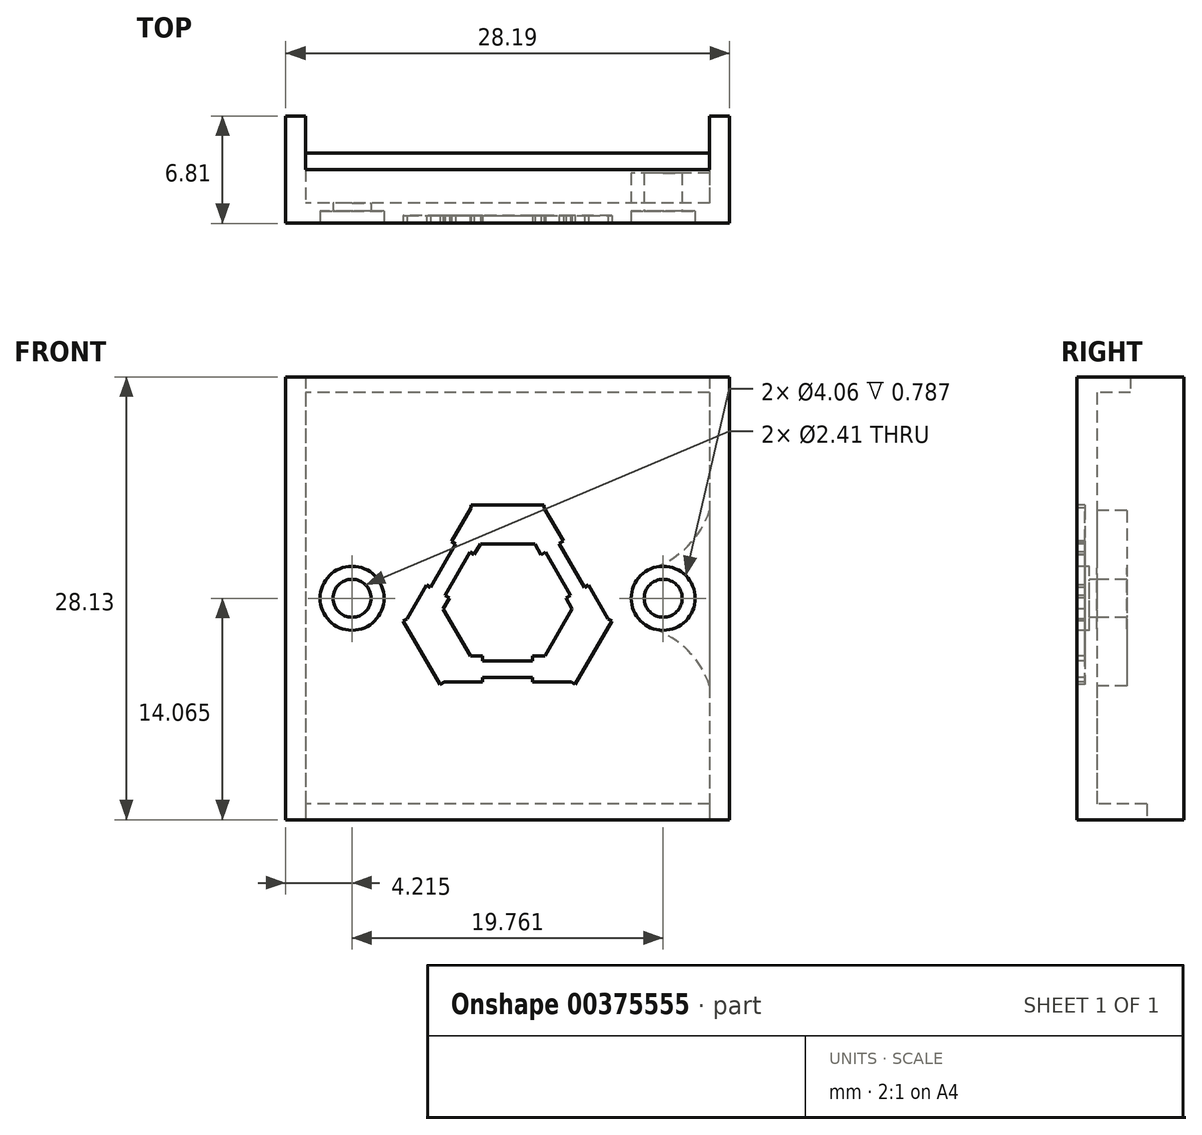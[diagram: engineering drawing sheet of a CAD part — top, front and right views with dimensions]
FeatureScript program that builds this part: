
annotation { "Feature Type Name" : "Feature", "Feature Type Description" : "" }
export const myFeature = defineFeature(function(context is Context, id is Id, definition is map)
    precondition{}
    {
        {
            var Q0;
            Q0=qCreatedBy(makeId("Top.planeOp"),FACE);
            var sketch = newSketch(context, id + "F0", { "sketchPlane" : qUnion([Q0])});
            skLineSegment(sketch, "E0", {"start": v(-22.88, 2.03) * mm, "end": v(-22.88, -1.6) * mm});
            skLineSegment(sketch, "E1", {"start": v(-22.88, -1.6) * mm, "end": v(2.77, -1.6) * mm});
            skLineSegment(sketch, "E2", {"start": v(2.77, -1.6) * mm, "end": v(2.77, 2.03) * mm});
            skLineSegment(sketch, "E3.0", {"start": v(4.04, -2.88) * mm, "end": v(4.04, 2.03) * mm});
            skLineSegment(sketch, "E3.1", {"start": v(-24.15, -2.88) * mm, "end": v(4.04, -2.88) * mm});
            skLineSegment(sketch, "E3.2", {"start": v(-24.15, 2.03) * mm, "end": v(-24.15, -2.88) * mm});
            skLineSegment(sketch, "E4", {"start": v(-24.15, 2.03) * mm, "end": v(-22.88, 2.03) * mm});
            skLineSegment(sketch, "E5", {"start": v(2.77, 2.03) * mm, "end": v(4.04, 2.03) * mm});
            skSolve(sketch);
        }
        {
            var Q0;
            Q0=makeQuery(id+"F0.imprint","IMPRINT",FACE,{"disambiguationData":[TD([[makeQuery(id+"F0.imprint","IMPRINT",EDGE,{"derivedFrom":sQuery(id+"F0.wireOp",EDGE,"E0")}),-1.0]])]});
            extrude(context, id + "F1", {"entities" : qUnion([Q0]), "depth" : 24.13 * mm});
        }
        {
            var Q0;
            Q0=makeQuery(id+"F1.opExtrude","SWEPT_FACE",FACE,{"disambiguationData":[OSD([sQuery(id+"F0.wireOp",EDGE,"E3.1")])]});
            var sketch = newSketch(context, id + "F2", { "sketchPlane" : qUnion([Q0])});
            skLineSegment(sketch, "E6", {"start": v(-10.05, 24.13) * mm, "end": v(-10.05, 0) * mm, "construction": true});
            skLineSegment(sketch, "E7", {"start": v(-19.94, 12.07) * mm, "end": v(-0.17, 12.07) * mm, "construction": true});
            skCircle(sketch, "E8", {"center": v(-19.94, 12.06) * mm, "radius": 2.03 * mm});
            skCircle(sketch, "E9", {"center": v(-0.17, 12.06) * mm, "radius": 2.03 * mm});
            skPoint(sketch, "E10.orphan", {"position": v(-24.15, 12.07) * mm});
            skPoint(sketch, "E11.orphan", {"position": v(4.04, 12.06) * mm});
            skPoint(sketch, "E12", {"position": v(-10.05, 12.06) * mm});
            skCircle(sketch, "E13", {"center": v(-19.94, 12.06) * mm, "radius": 1.2 * mm});
            skCircle(sketch, "E14", {"center": v(-0.17, 12.06) * mm, "radius": 1.2 * mm});
            skSolve(sketch);
        }
        {
            var Q0;
            Q0=makeQuery(id+"F2.imprint","IMPRINT",FACE,{"disambiguationData":[TD([[makeQuery(id+"F2.imprint","IMPRINT",EDGE,{"derivedFrom":sQuery(id+"F2.wireOp",EDGE,"E8")}),1.0]])]});
            var Q1;
            Q1=makeQuery(id+"F2.imprint","IMPRINT",FACE,{"disambiguationData":[TD([[makeQuery(id+"F2.imprint","IMPRINT",EDGE,{"derivedFrom":sQuery(id+"F2.wireOp",EDGE,"E9")}),1.0]])]});
            extrude(context, id + "F3", {"entities" : qUnion([Q0, Q1]), "operationType" : NewBodyOperationType.REMOVE, "oppositeDirection" : true, "depth" : 0.79 * mm});
        }
        {
            var Q0;
            Q0=makeQuery(id+"F3.boolean.opBoolean","SPLIT",FACE,{"disambiguationData":[TD([makeQuery(id+"F3.opExtrude","SWEPT_FACE",FACE,{"disambiguationData":[OSD([sQuery(id+"F2.wireOp",EDGE,"E13")])]})])],"derivedFrom":makeQuery(id+"F1.opExtrude","SWEPT_FACE",FACE,{"disambiguationData":[OSD([sQuery(id+"F0.wireOp",EDGE,"E3.1")])]})});
            var Q1;
            Q1=makeQuery(id+"F3.boolean.opBoolean","SPLIT",FACE,{"disambiguationData":[TD([makeQuery(id+"F3.opExtrude","SWEPT_FACE",FACE,{"disambiguationData":[OSD([sQuery(id+"F2.wireOp",EDGE,"E14")])]})])],"derivedFrom":makeQuery(id+"F1.opExtrude","SWEPT_FACE",FACE,{"disambiguationData":[OSD([sQuery(id+"F0.wireOp",EDGE,"E3.1")])]})});
            extrude(context, id + "F4", {"entities" : qUnion([Q0, Q1]), "operationType" : NewBodyOperationType.REMOVE, "oppositeDirection" : true, "depth" : 25.4 * mm});
        }
        {
            var Q0;
            {var subQ0=sQuery(id+"F0.wireOp",EDGE,"E3.0");var subQ4=sQuery(id+"F0.wireOp",EDGE,"E3.1");Q0=makeQuery(id+"F3.boolean.opBoolean","SPLIT",FACE,{"disambiguationData":[TD([makeQuery(id+"F1.opExtrude","SWEPT_FACE",FACE,{"disambiguationData":[OSD([subQ0])]})])],"derivedFrom":makeQuery(id+"F1.opExtrude","SWEPT_FACE",FACE,{"disambiguationData":[OSD([subQ4])]})});}
            var sketch = newSketch(context, id + "F5", { "sketchPlane" : qUnion([Q0])});
            skLineSegment(sketch, "E15", {"start": v(-10.05, 24.13) * mm, "end": v(-10.05, 0) * mm, "construction": true});
            skPoint(sketch, "E16", {"position": v(-10.05, 6.37) * mm});
            skLineSegment(sketch, "E17", {"start": v(-13.6, 15.68) * mm, "end": v(-12.4, 17.81) * mm});
            skLineSegment(sketch, "E18", {"start": v(-12.4, 17.81) * mm, "end": v(-12.4, 17.97) * mm});
            skLineSegment(sketch, "E19", {"start": v(-12.4, 17.97) * mm, "end": v(-7.74, 17.97) * mm});
            skLineSegment(sketch, "E20", {"start": v(-7.74, 17.97) * mm, "end": v(-7.74, 17.81) * mm});
            skLineSegment(sketch, "E21", {"start": v(-7.74, 17.81) * mm, "end": v(-6.51, 15.7) * mm});
            skLineSegment(sketch, "E22", {"start": v(-6.51, 15.7) * mm, "end": v(-6.78, 15.53) * mm});
            skLineSegment(sketch, "E23", {"start": v(-6.78, 15.53) * mm, "end": v(-5.18, 12.76) * mm});
            skLineSegment(sketch, "E24", {"start": v(-5.18, 12.76) * mm, "end": v(-4.92, 12.91) * mm});
            skLineSegment(sketch, "E25", {"start": v(-4.92, 12.91) * mm, "end": v(-3.68, 10.76) * mm});
            skLineSegment(sketch, "E26", {"start": v(-3.68, 10.76) * mm, "end": v(-3.44, 10.64) * mm});
            skLineSegment(sketch, "E27", {"start": v(-3.44, 10.64) * mm, "end": v(-5.76, 6.6) * mm});
            skLineSegment(sketch, "E28", {"start": v(-5.76, 6.6) * mm, "end": v(-6, 6.74) * mm});
            skLineSegment(sketch, "E29", {"start": v(-6, 6.74) * mm, "end": v(-8.47, 6.74) * mm});
            skLineSegment(sketch, "E30", {"start": v(-8.47, 6.74) * mm, "end": v(-8.47, 7.04) * mm});
            skLineSegment(sketch, "E31", {"start": v(-8.47, 7.04) * mm, "end": v(-11.65, 7.04) * mm});
            skLineSegment(sketch, "E32", {"start": v(-11.65, 7.04) * mm, "end": v(-11.65, 6.74) * mm});
            skLineSegment(sketch, "E33", {"start": v(-11.65, 6.74) * mm, "end": v(-14.07, 6.74) * mm});
            skLineSegment(sketch, "E34", {"start": v(-14.07, 6.74) * mm, "end": v(-14.35, 6.58) * mm});
            skLineSegment(sketch, "E35", {"start": v(-14.35, 6.58) * mm, "end": v(-16.68, 10.62) * mm});
            skLineSegment(sketch, "E36", {"start": v(-16.68, 10.62) * mm, "end": v(-16.45, 10.76) * mm});
            skLineSegment(sketch, "E37", {"start": v(-16.45, 10.76) * mm, "end": v(-15.22, 12.91) * mm});
            skLineSegment(sketch, "E38", {"start": v(-15.22, 12.91) * mm, "end": v(-14.94, 12.76) * mm});
            skLineSegment(sketch, "E39", {"start": v(-14.94, 12.76) * mm, "end": v(-13.35, 15.53) * mm});
            skLineSegment(sketch, "E40", {"start": v(-13.35, 15.53) * mm, "end": v(-13.6, 15.68) * mm});
            skLineSegment(sketch, "E41", {"start": v(-11.79, 15.5) * mm, "end": v(-8.33, 15.5) * mm});
            skLineSegment(sketch, "E42", {"start": v(-8.33, 15.5) * mm, "end": v(-7.94, 14.83) * mm});
            skLineSegment(sketch, "E43", {"start": v(-7.94, 14.83) * mm, "end": v(-7.65, 15) * mm});
            skLineSegment(sketch, "E44", {"start": v(-7.65, 15) * mm, "end": v(-6.06, 12.25) * mm});
            skLineSegment(sketch, "E45", {"start": v(-6.06, 12.25) * mm, "end": v(-6.36, 12.07) * mm});
            skLineSegment(sketch, "E46", {"start": v(-6.36, 12.07) * mm, "end": v(-5.97, 11.4) * mm});
            skLineSegment(sketch, "E47", {"start": v(-5.97, 11.4) * mm, "end": v(-7.69, 8.4) * mm});
            skLineSegment(sketch, "E48", {"start": v(-7.69, 8.4) * mm, "end": v(-8.47, 8.4) * mm});
            skLineSegment(sketch, "E49", {"start": v(-8.47, 8.4) * mm, "end": v(-8.47, 8.08) * mm});
            skLineSegment(sketch, "E50", {"start": v(-8.47, 8.08) * mm, "end": v(-11.64, 8.08) * mm});
            skLineSegment(sketch, "E51", {"start": v(-11.64, 8.08) * mm, "end": v(-11.64, 8.39) * mm});
            skLineSegment(sketch, "E52", {"start": v(-11.64, 8.39) * mm, "end": v(-12.41, 8.39) * mm});
            skLineSegment(sketch, "E53", {"start": v(-12.41, 8.39) * mm, "end": v(-14.15, 11.39) * mm});
            skLineSegment(sketch, "E54", {"start": v(-14.15, 11.39) * mm, "end": v(-13.76, 12.07) * mm});
            skLineSegment(sketch, "E55", {"start": v(-13.76, 12.07) * mm, "end": v(-14.04, 12.23) * mm});
            skLineSegment(sketch, "E56", {"start": v(-14.04, 12.23) * mm, "end": v(-12.46, 15) * mm});
            skLineSegment(sketch, "E57", {"start": v(-12.46, 15) * mm, "end": v(-12.18, 14.84) * mm});
            skLineSegment(sketch, "E58", {"start": v(-12.18, 14.84) * mm, "end": v(-11.79, 15.5) * mm});
            skSolve(sketch);
        }
        {
            var Q0;
            Q0=makeQuery(id+"F5.imprint","IMPRINT",FACE,{"disambiguationData":[TD([[makeQuery(id+"F5.imprint","IMPRINT",EDGE,{"derivedFrom":sQuery(id+"F5.wireOp",EDGE,"E17")}),-1.0]])]});
            extrude(context, id + "F6", {"entities" : qUnion([Q0]), "operationType" : NewBodyOperationType.REMOVE, "oppositeDirection" : true, "depth" : .5 * mm});
        }
        {
            var Q0;
            Q0=makeQuery(id+"F1.opExtrude","CAP_FACE",FACE,{"disambiguationData":[OSD([sQuery(id+"F0.wireOp",EDGE,"E0"),sQuery(id+"F0.wireOp",EDGE,"E1"),sQuery(id+"F0.wireOp",EDGE,"E2"),sQuery(id+"F0.wireOp",EDGE,"E3.0"),sQuery(id+"F0.wireOp",EDGE,"E3.1"),sQuery(id+"F0.wireOp",EDGE,"E3.2"),sQuery(id+"F0.wireOp",EDGE,"E4"),sQuery(id+"F0.wireOp",EDGE,"E5")])],"isStart":true});
            extrude(context, id + "F7", {"entities" : qUnion([Q0]), "operationType" : NewBodyOperationType.ADD, "depth" : 2 * mm});
        }
        {
            var Q0;
            Q0=makeQuery(id+"F1.opExtrude","CAP_FACE",FACE,{"disambiguationData":[OSD([sQuery(id+"F0.wireOp",EDGE,"E0"),sQuery(id+"F0.wireOp",EDGE,"E1"),sQuery(id+"F0.wireOp",EDGE,"E2"),sQuery(id+"F0.wireOp",EDGE,"E3.0"),sQuery(id+"F0.wireOp",EDGE,"E3.1"),sQuery(id+"F0.wireOp",EDGE,"E3.2"),sQuery(id+"F0.wireOp",EDGE,"E4"),sQuery(id+"F0.wireOp",EDGE,"E5")])],"isStart":false});
            extrude(context, id + "F8", {"entities" : qUnion([Q0]), "operationType" : NewBodyOperationType.ADD, "depth" : 2 * mm});
        }
        {
            var Q0;
            {var subQ0=sQuery(id+"F0.wireOp",EDGE,"E1");Q0=makeQuery(id+"F8.boolean.opBoolean","MERGE",FACE,{"derivedFrom":[makeQuery(id+"F7.boolean.opBoolean","MERGE",FACE,{"derivedFrom":[makeQuery(id+"F1.opExtrude","SWEPT_FACE",FACE,{"disambiguationData":[OSD([subQ0])]}),makeQuery(id+"F7.opExtrude","SWEPT_FACE",FACE,{"disambiguationData":[OSD([subQ0])]})]}),makeQuery(id+"F8.opExtrude","SWEPT_FACE",FACE,{"disambiguationData":[OSD([subQ0])]})]});}
            var sketch = newSketch(context, id + "F9", { "sketchPlane" : qUnion([Q0])});
            skLineSegment(sketch, "E59.top", {"start": v(-2.77, 24.13) * mm, "end": v(22.88, 24.13) * mm, "construction": true});
            skLineSegment(sketch, "E59.left", {"start": v(-2.77, 26.13) * mm, "end": v(-2.77, 24.13) * mm, "construction": true});
            skLineSegment(sketch, "E59.right", {"start": v(22.88, 26.13) * mm, "end": v(22.88, 24.13) * mm, "construction": true});
            skLineSegment(sketch, "E60.bottom", {"start": v(-2.77, 26.13) * mm, "end": v(22.88, 26.13) * mm});
            skLineSegment(sketch, "E60.top", {"start": v(-2.77, 25.13) * mm, "end": v(22.88, 25.13) * mm});
            skLineSegment(sketch, "E60.left", {"start": v(-2.77, 26.13) * mm, "end": v(-2.77, 25.13) * mm});
            skLineSegment(sketch, "E60.right", {"start": v(22.88, 26.13) * mm, "end": v(22.88, 25.13) * mm});
            skLineSegment(sketch, "E61", {"start": v(-2.77, 12.07) * mm, "end": v(7.16, 12.07) * mm, "construction": true});
            skLineSegment(sketch, "E62.MirrorCS", {"start": v(-2.77, -1) * mm, "end": v(22.88, -1) * mm});
            skLineSegment(sketch, "E63.MirrorCS", {"start": v(-2.77, -2) * mm, "end": v(22.88, -2) * mm});
            skLineSegment(sketch, "E64", {"start": v(-2.77, -1) * mm, "end": v(-2.77, -2) * mm});
            skLineSegment(sketch, "E65", {"start": v(22.88, -1) * mm, "end": v(22.88, -2) * mm});
            skSolve(sketch);
        }
        {
            var Q0;
            Q0=makeQuery(id+"F9.imprint","IMPRINT",FACE,{"disambiguationData":[TD([[makeQuery(id+"F9.imprint","IMPRINT",EDGE,{"derivedFrom":sQuery(id+"F9.wireOp",EDGE,"E60.bottom")}),1.0]])]});
            var Q1;
            Q1=makeQuery(id+"F9.imprint","IMPRINT",FACE,{"disambiguationData":[TD([[makeQuery(id+"F9.imprint","IMPRINT",EDGE,{"derivedFrom":sQuery(id+"F9.wireOp",EDGE,"E62.MirrorCS")}),-1.0]])]});
            extrude(context, id + "F10", {"entities" : qUnion([Q0, Q1]), "operationType" : NewBodyOperationType.ADD, "depth" : 1.27 * mm});
        }
        {
            var Q0;
            {var subQ0=sQuery(id+"F0.wireOp",EDGE,"E1");Q0=makeQuery(id+"F8.boolean.opBoolean","MERGE",FACE,{"derivedFrom":[makeQuery(id+"F7.boolean.opBoolean","MERGE",FACE,{"derivedFrom":[makeQuery(id+"F1.opExtrude","SWEPT_FACE",FACE,{"disambiguationData":[OSD([subQ0])]}),makeQuery(id+"F7.opExtrude","SWEPT_FACE",FACE,{"disambiguationData":[OSD([subQ0])]})]}),makeQuery(id+"F8.opExtrude","SWEPT_FACE",FACE,{"disambiguationData":[OSD([subQ0])]})]});}
            var sketch = newSketch(context, id + "F11", { "sketchPlane" : qUnion([Q0])});
            skLineSegment(sketch, "E66", {"start": v(20.32, 12.06) * mm, "end": v(19.81, 12.06) * mm, "construction": true});
            skLineSegment(sketch, "E67", {"start": v(10.05, -1) * mm, "end": v(10.05, 25.13) * mm, "construction": true});
            skArc(sketch, "E68.0", {"start": v(0.83, 10.13) * mm, "mid": v(2.22, 12.06) * mm, "end": v(0.83, 14) * mm});
            skArc(sketch, "E69", {"start": v(-2.77, 17.63) * mm, "mid": v(-1.4, 15.4) * mm, "end": v(0.83, 14) * mm});
            skLineSegment(sketch, "E70", {"start": v(0.17, 12.06) * mm, "end": v(0, 12.06) * mm, "construction": true});
            skArc(sketch, "E71.MirrorCS", {"start": v(-2.77, 6.5) * mm, "mid": v(-1.4, 8.74) * mm, "end": v(0.83, 10.13) * mm});
            skArc(sketch, "E72.MirrorCS", {"start": v(22.88, 17.63) * mm, "mid": v(21.51, 15.4) * mm, "end": v(19.28, 14) * mm});
            skArc(sketch, "E73.MirrorCS", {"start": v(19.28, 10.13) * mm, "mid": v(17.9, 12.07) * mm, "end": v(19.28, 14) * mm});
            skArc(sketch, "E74.MirrorCS", {"start": v(22.88, 6.5) * mm, "mid": v(21.51, 8.74) * mm, "end": v(19.28, 10.13) * mm});
            skLineSegment(sketch, "E75", {"start": v(-2.77, 17.63) * mm, "end": v(-2.77, 6.5) * mm});
            skLineSegment(sketch, "E76", {"start": v(22.88, 17.63) * mm, "end": v(22.88, 6.5) * mm});
            skLineSegment(sketch, "E77", {"start": v(-2.77, 17.63) * mm, "end": v(-2.77, 25.13) * mm});
            skLineSegment(sketch, "E78", {"start": v(-2.77, 25.13) * mm, "end": v(22.88, 25.13) * mm});
            skLineSegment(sketch, "E79", {"start": v(22.88, 25.13) * mm, "end": v(22.88, 17.63) * mm});
            skLineSegment(sketch, "E80", {"start": v(22.88, 6.5) * mm, "end": v(22.88, -1) * mm});
            skLineSegment(sketch, "E81", {"start": v(22.88, -1) * mm, "end": v(-2.77, -1) * mm});
            skLineSegment(sketch, "E82", {"start": v(-2.77, -1) * mm, "end": v(-2.77, 6.5) * mm});
            skCircle(sketch, "E83.0", {"center": v(0.17, 12.06) * mm, "radius": 1.2 * mm});
            skCircle(sketch, "E83.1", {"center": v(19.94, 12.06) * mm, "radius": 1.2 * mm});
            skSolve(sketch);
        }
        {
            var Q0;
            Q0=makeQuery(id+"F11.imprint","IMPRINT",FACE,{"disambiguationData":[TD([[makeQuery(id+"F11.imprint","IMPRINT",EDGE,{"derivedFrom":sQuery(id+"F11.wireOp",EDGE,"5b848598-8b62-4473-9078-29c7f42ded91.0")}),1.0]])]});
            var Q1;
            Q1=makeQuery(id+"F11.imprint","IMPRINT",FACE,{"disambiguationData":[TD([[makeQuery(id+"F11.imprint","IMPRINT",EDGE,{"derivedFrom":sQuery(id+"F11.wireOp",EDGE,"292e60b4-9bbb-43bc-9e86-de80fa0e97c2.0")}),1.0]])]});
            var Q2;
            Q2=makeQuery(id+"F11.imprint","IMPRINT",FACE,{"disambiguationData":[TD([[makeQuery(id+"F11.imprint","IMPRINT",EDGE,{"derivedFrom":sQuery(id+"F11.wireOp",EDGE,"E68.0")}),1.0]])]});
            var Q3;
            Q3=makeQuery(id+"F11.imprint","IMPRINT",FACE,{"disambiguationData":[TD([[makeQuery(id+"F11.imprint","IMPRINT",EDGE,{"derivedFrom":sQuery(id+"F11.wireOp",EDGE,"E72.MirrorCS")}),1.0]])]});
            extrude(context, id + "F12", {"entities" : qUnion([Q0, Q1, Q2, Q3]), "operationType" : NewBodyOperationType.ADD, "depth" : 1.9 * mm});
        }
        {
            var Q0;
            {var subQ0=sQuery(id+"F0.wireOp",EDGE,"E4");Q0=makeQuery(id+"F8.boolean.opBoolean","MERGE",FACE,{"derivedFrom":[makeQuery(id+"F7.boolean.opBoolean","MERGE",FACE,{"derivedFrom":[makeQuery(id+"F1.opExtrude","SWEPT_FACE",FACE,{"disambiguationData":[OSD([subQ0])]}),makeQuery(id+"F7.opExtrude","SWEPT_FACE",FACE,{"disambiguationData":[OSD([subQ0])]})]}),makeQuery(id+"F8.opExtrude","SWEPT_FACE",FACE,{"disambiguationData":[OSD([subQ0])]})]});}
            var Q1;
            Q1=makeQuery(id+"F10.opExtrude","CAP_FACE",FACE,{"disambiguationData":[OSD([sQuery(id+"F9.wireOp",EDGE,"E60.bottom"),sQuery(id+"F9.wireOp",EDGE,"E60.top"),sQuery(id+"F9.wireOp",EDGE,"E60.left"),sQuery(id+"F9.wireOp",EDGE,"E60.right")])],"isStart":false});
            var Q2;
            Q2=makeQuery(id+"F10.opExtrude","CAP_FACE",FACE,{"disambiguationData":[OSD([sQuery(id+"F9.wireOp",EDGE,"E62.MirrorCS"),sQuery(id+"F9.wireOp",EDGE,"E64"),sQuery(id+"F9.wireOp",EDGE,"E63.MirrorCS"),sQuery(id+"F9.wireOp",EDGE,"E65")])],"isStart":false});
            var Q3;
            {var subQ0=sQuery(id+"F0.wireOp",EDGE,"E5");Q3=makeQuery(id+"F8.boolean.opBoolean","MERGE",FACE,{"derivedFrom":[makeQuery(id+"F7.boolean.opBoolean","MERGE",FACE,{"derivedFrom":[makeQuery(id+"F1.opExtrude","SWEPT_FACE",FACE,{"disambiguationData":[OSD([subQ0])]}),makeQuery(id+"F7.opExtrude","SWEPT_FACE",FACE,{"disambiguationData":[OSD([subQ0])]})]}),makeQuery(id+"F8.opExtrude","SWEPT_FACE",FACE,{"disambiguationData":[OSD([subQ0])]})]});}
            extrude(context, id + "F13", {"entities" : qUnion([Q0, Q1, Q2, Q3]), "operationType" : NewBodyOperationType.ADD, "depth" : 1.9 * mm});
        }
        {
            var Q0;
            Q0=makeQuery(id+"F13.opExtrude","CAP_FACE",FACE,{"disambiguationData":[OSD([sQuery(id+"F9.wireOp",EDGE,"E60.bottom"),sQuery(id+"F9.wireOp",EDGE,"E60.top"),sQuery(id+"F9.wireOp",EDGE,"E60.left"),sQuery(id+"F9.wireOp",EDGE,"E60.right")])],"isStart":false});
            extrude(context, id + "F14", {"entities" : qUnion([Q0]), "operationType" : NewBodyOperationType.REMOVE, "oppositeDirection" : true, "depth" : 1.04 * mm});
        }
    });
